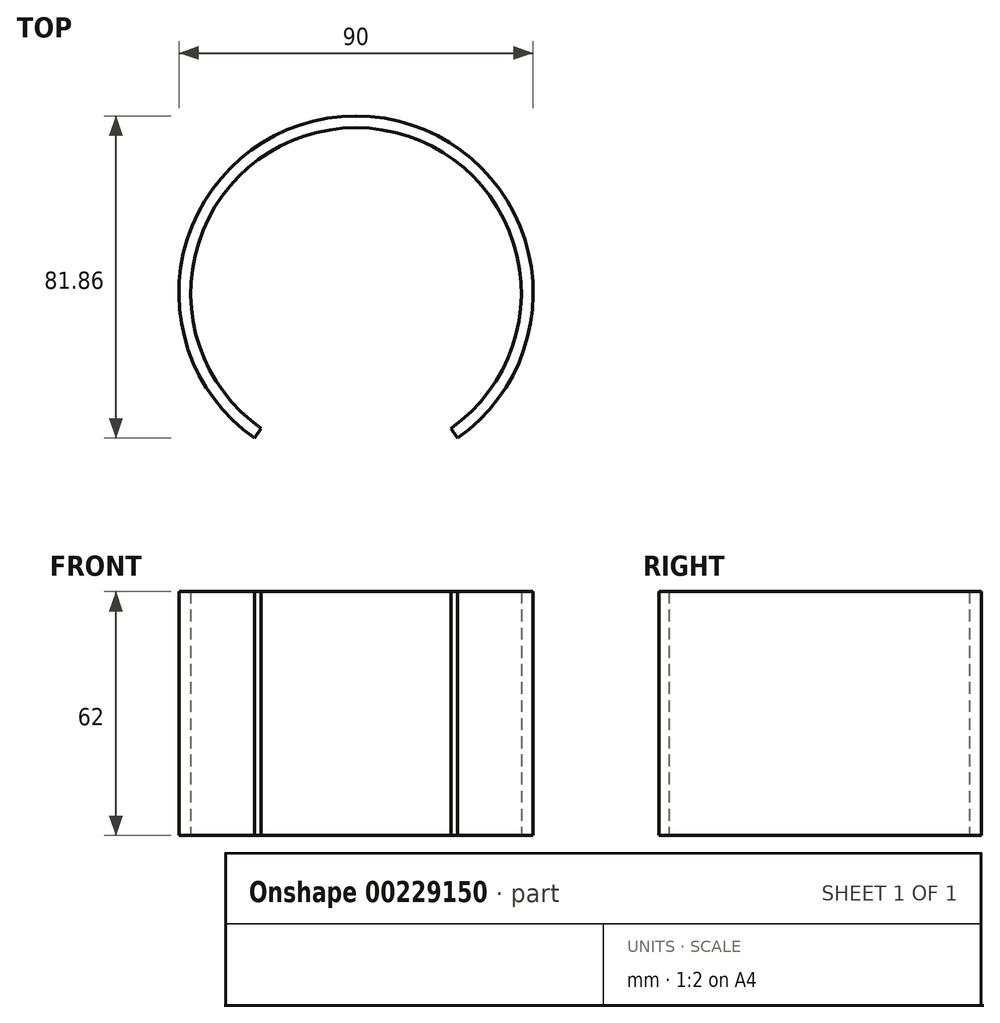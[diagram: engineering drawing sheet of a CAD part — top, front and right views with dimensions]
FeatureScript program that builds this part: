
annotation { "Feature Type Name" : "Feature", "Feature Type Description" : "" }
export const myFeature = defineFeature(function(context is Context, id is Id, definition is map)
    precondition{}
    {
        {
            var Q0;
            Q0=qCreatedBy(makeId("Top.planeOp"),FACE);
            var sketch = newSketch(context, id + "F0", { "sketchPlane" : qUnion([Q0])});
            skArc(sketch, "E0", {"start": v(25.81, -36.86) * mm, "mid": v(44.83, 3.92) * mm, "end": v(19.02, 40.78) * mm});
            skArc(sketch, "E1", {"start": v(24.09, -34.4) * mm, "mid": v(0, 42) * mm, "end": v(-24.09, -34.4) * mm});
            skLineSegment(sketch, "E2", {"start": v(24.09, -34.4) * mm, "end": v(25.81, -36.86) * mm});
            skLineSegment(sketch, "E3", {"start": v(0, -60.58) * mm, "end": v(0, 54.66) * mm, "construction": true});
            skLineSegment(sketch, "E4.MirrorCS", {"start": v(-24.09, -34.4) * mm, "end": v(-25.81, -36.86) * mm});
            skArc(sketch, "E5", {"start": v(-21.24, 38.9) * mm, "mid": v(-38.37, 22.15) * mm, "end": v(-44.3, -1.06) * mm});
            skLineSegment(sketch, "E6", {"start": v(-18.73, 40.16) * mm, "end": v(-19.02, 40.78) * mm});
            skLineSegment(sketch, "E7", {"start": v(-44.14, -3.86) * mm, "end": v(-44.83, -3.92) * mm});
            skLineSegment(sketch, "E8", {"start": v(0, 0) * mm, "end": v(-69.84, -40.32) * mm, "construction": true});
            skArc(sketch, "E9.trimOffspring", {"start": v(-19.02, 40.78) * mm, "mid": v(-44.83, 3.92) * mm, "end": v(-25.81, -36.86) * mm});
            skLineSegment(sketch, "E10.MirrorCS", {"start": v(18.73, 40.16) * mm, "end": v(19.02, 40.78) * mm});
            skLineSegment(sketch, "E11.MirrorCS", {"start": v(44.14, -3.86) * mm, "end": v(44.83, -3.92) * mm});
            skArc(sketch, "E12.trimOffspring", {"start": v(19.02, 40.78) * mm, "mid": v(0, 45) * mm, "end": v(-19.02, 40.78) * mm});
            skPoint(sketch, "E13.orphan", {"position": v(-17.75, 38.06) * mm});
            skPoint(sketch, "E14.orphan", {"position": v(17.75, 38.06) * mm});
            skPoint(sketch, "E15.orphan", {"position": v(-41.84, -3.66) * mm});
            skPoint(sketch, "E16.orphan", {"position": v(41.84, -3.66) * mm});
            skPoint(sketch, "E17.visualSharp", {"position": v(-18.73, 40.16) * mm});
            skPoint(sketch, "E18.visualSharp", {"position": v(18.73, 40.16) * mm});
            skPoint(sketch, "E19.visualSharp", {"position": v(44.14, -3.86) * mm});
            skPoint(sketch, "E20.visualSharp", {"position": v(-44.14, -3.86) * mm});
            skArc(sketch, "E21.converted", {"start": v(44.14, -3.86) * mm, "mid": v(38.37, 22.15) * mm, "end": v(18.73, 40.16) * mm});
            skArc(sketch, "E22.trimOffspring", {"start": v(-18.73, 40.16) * mm, "mid": v(-38.37, 22.16) * mm, "end": v(-44.14, -3.86) * mm});
            skSolve(sketch);
        }
        {
            var Q0;
            Q0=qSketchRegion(id+"F0",true);
            extrude(context, id + "F1", {"entities" : qUnion([Q0]), "depth" : 62 * mm, "offsetDistance" : 25 * mm});
        }
    });
